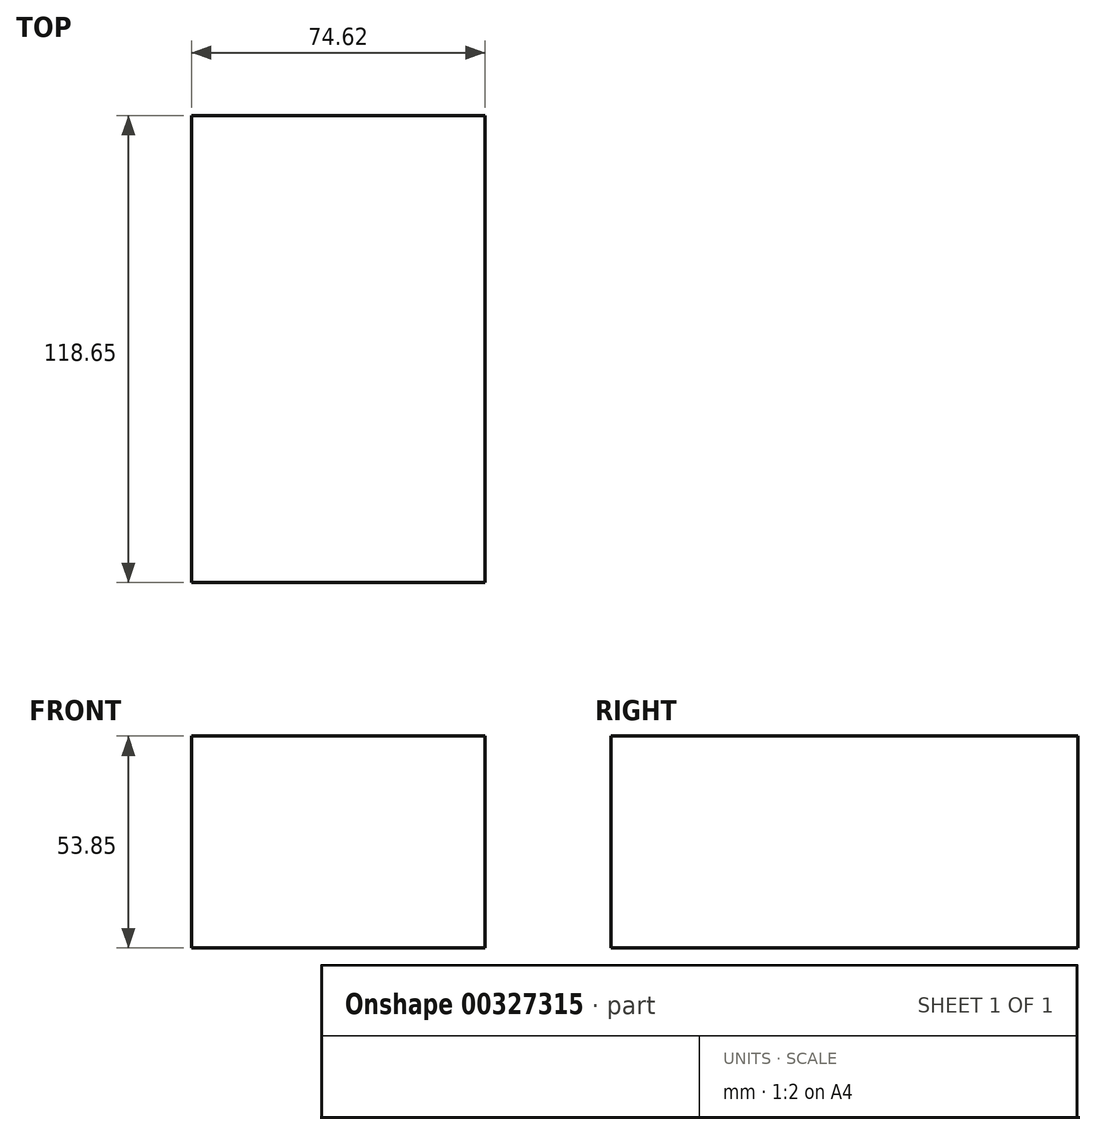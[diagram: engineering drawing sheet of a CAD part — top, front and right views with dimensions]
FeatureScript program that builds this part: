
annotation { "Feature Type Name" : "Feature", "Feature Type Description" : "" }
export const myFeature = defineFeature(function(context is Context, id is Id, definition is map)
    precondition{}
    {
        {
            var Q0;
            Q0=qCreatedBy(makeId("Top.planeOp"),FACE);
            var sketch = newSketch(context, id + "F0", { "sketchPlane" : qUnion([Q0])});
            skLineSegment(sketch, "E0.bottom", {"start": v(-64.58, 78.01) * mm, "end": v(10.04, 78.01) * mm});
            skLineSegment(sketch, "E0.top", {"start": v(-64.58, -40.64) * mm, "end": v(10.04, -40.64) * mm});
            skLineSegment(sketch, "E0.left", {"start": v(-64.58, 78.01) * mm, "end": v(-64.58, -40.64) * mm});
            skLineSegment(sketch, "E0.right", {"start": v(10.04, 78.01) * mm, "end": v(10.04, -40.64) * mm});
            skSolve(sketch);
        }
        {
            var Q0;
            Q0=makeQuery(id+"F0.imprint","IMPRINT",FACE,{"disambiguationData":[TD([[makeQuery(id+"F0.imprint","IMPRINT",EDGE,{"derivedFrom":sQuery(id+"F0.wireOp",EDGE,"E0.bottom")}),-1.0]])]});
            extrude(context, id + "F1", {"entities" : qUnion([Q0]), "depth" : 53.85 * mm});
        }
    });
